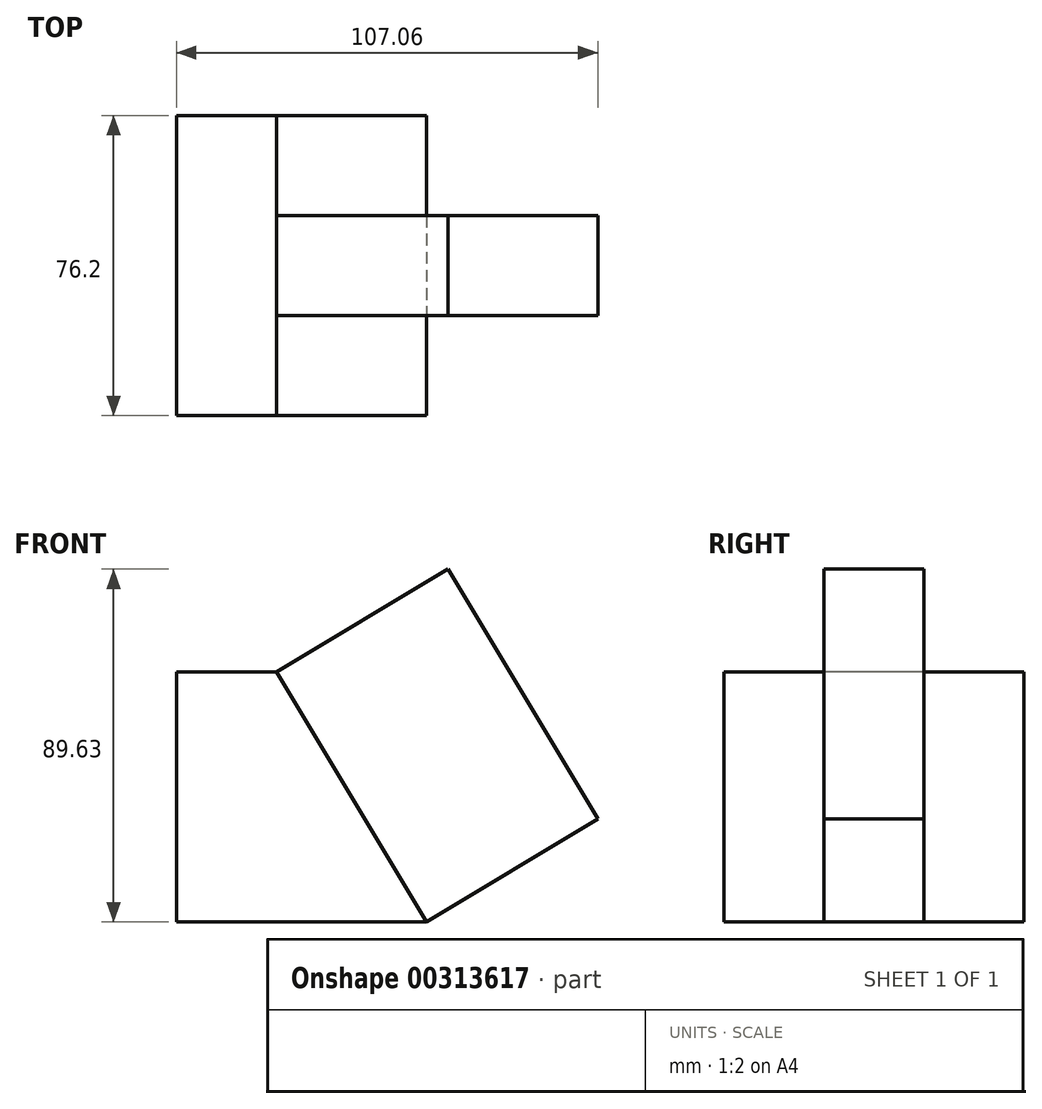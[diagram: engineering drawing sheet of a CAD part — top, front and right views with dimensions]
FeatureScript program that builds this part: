
annotation { "Feature Type Name" : "Feature", "Feature Type Description" : "" }
export const myFeature = defineFeature(function(context is Context, id is Id, definition is map)
    precondition{}
    {
        {
            var Q0;
            Q0=qCreatedBy(makeId("Front.planeOp"),FACE);
            var sketch = newSketch(context, id + "F0", { "sketchPlane" : qUnion([Q0])});
            skLineSegment(sketch, "E0", {"start": v(-32.83, -32.03) * mm, "end": v(30.67, -32.03) * mm});
            skLineSegment(sketch, "E1", {"start": v(-32.83, -32.03) * mm, "end": v(-32.83, 31.47) * mm});
            skLineSegment(sketch, "E2", {"start": v(-32.83, 31.47) * mm, "end": v(-7.43, 31.47) * mm});
            skLineSegment(sketch, "E3", {"start": v(-7.43, 31.47) * mm, "end": v(30.67, -32.03) * mm});
            skSolve(sketch);
        }
        {
            var Q0;
            Q0=makeQuery(id+"F0.imprint","IMPRINT",FACE,{"disambiguationData":[TD([[makeQuery(id+"F0.imprint","IMPRINT",EDGE,{"derivedFrom":sQuery(id+"F0.wireOp",EDGE,"E0")}),1.0]])]});
            extrude(context, id + "F1", {"entities" : qUnion([Q0]), "oppositeDirection" : true, "depth" : 76.2 * mm});
        }
        {
            var Q0;
            Q0=makeQuery(id+"F1.opExtrude","SWEPT_FACE",FACE,{"disambiguationData":[OSD([sQuery(id+"F0.wireOp",EDGE,"E3")])]});
            var sketch = newSketch(context, id + "F2", { "sketchPlane" : qUnion([Q0])});
            skLineSegment(sketch, "E4", {"start": v(0, -43.25) * mm, "end": v(25.4, -43.25) * mm});
            skLineSegment(sketch, "E5", {"start": v(25.4, -43.25) * mm, "end": v(25.4, 30.8) * mm});
            skLineSegment(sketch, "E6", {"start": v(76.2, -43.25) * mm, "end": v(50.8, -43.25) * mm});
            skLineSegment(sketch, "E7", {"start": v(50.8, -43.25) * mm, "end": v(50.8, 30.8) * mm});
            skSolve(sketch);
        }
        {
            var Q0;
            {var subQ0=sQuery(id+"F2.wireOp",EDGE,"E5");Q0=makeQuery(id+"F2.imprint","IMPRINT",FACE,{"disambiguationData":[TD([[makeQuery(id+"F2.imprint","IMPRINT",EDGE,{"derivedFrom":subQ0}),-1.0]])]});}
            extrude(context, id + "F3", {"entities" : qUnion([Q0]), "operationType" : NewBodyOperationType.ADD, "depth" : 50.8 * mm});
        }
    });
